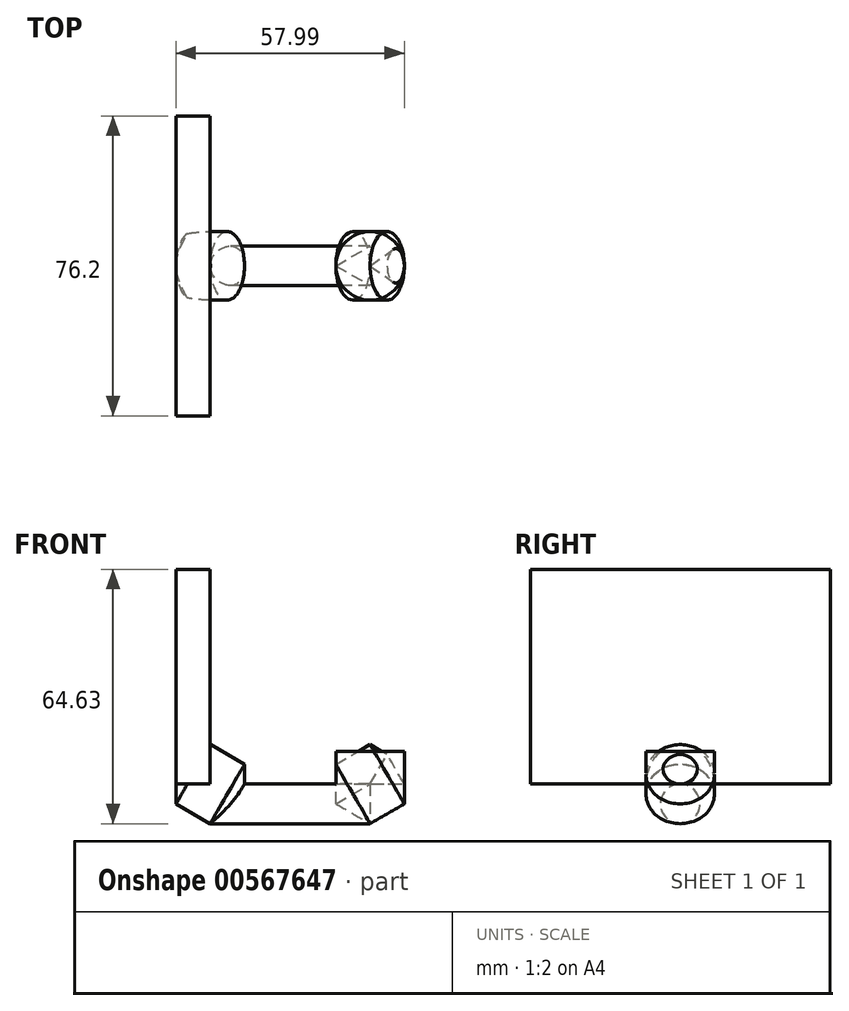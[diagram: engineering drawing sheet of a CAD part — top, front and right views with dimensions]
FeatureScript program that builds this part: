
annotation { "Feature Type Name" : "Feature", "Feature Type Description" : "" }
export const myFeature = defineFeature(function(context is Context, id is Id, definition is map)
    precondition{}
    {
        {
            var Q0;
            Q0=qCreatedBy(makeId("Front.planeOp"),FACE);
            var sketch = newSketch(context, id + "F0", { "sketchPlane" : qUnion([Q0])});
            skLineSegment(sketch, "E0", {"start": v(0, 5.02) * mm, "end": v(0, 64.63) * mm});
            skLineSegment(sketch, "E1", {"start": v(0, 64.63) * mm, "end": v(8.69, 64.63) * mm});
            skLineSegment(sketch, "E2", {"start": v(8.69, 64.63) * mm, "end": v(8.69, 0) * mm});
            skLineSegment(sketch, "E3", {"start": v(49.3, 0) * mm, "end": v(8.69, 0) * mm});
            skLineSegment(sketch, "E4", {"start": v(49.3, 5.02) * mm, "end": v(40.62, 5.02) * mm});
            skLineSegment(sketch, "E5", {"start": v(58, 10.05) * mm, "end": v(58, 5.02) * mm});
            skLineSegment(sketch, "E6", {"start": v(49.3, 18.37) * mm, "end": v(58, 18.37) * mm});
            skLineSegment(sketch, "E7", {"start": v(49.3, 5.02) * mm, "end": v(49.3, 18.37) * mm});
            skLineSegment(sketch, "E8", {"start": v(0, 5.02) * mm, "end": v(8.69, 5.02) * mm});
            skLineSegment(sketch, "E9", {"start": v(49.3, 0) * mm, "end": v(49.3, 5.02) * mm});
            skLineSegment(sketch, "E10", {"start": v(58, 10.05) * mm, "end": v(49.3, 10.05) * mm});
            skLineSegment(sketch, "E11", {"start": v(58, 18.37) * mm, "end": v(58, 10.05) * mm});
            skLineSegment(sketch, "E12", {"start": v(0, 5.02) * mm, "end": v(8.69, 0) * mm});
            skLineSegment(sketch, "E13", {"start": v(58, 5.02) * mm, "end": v(49.3, 0) * mm});
            skLineSegment(sketch, "E14.trimOffspring", {"start": v(17.37, 5.02) * mm, "end": v(8.69, 5.02) * mm});
            skLineSegment(sketch, "E15", {"start": v(17.37, 5.02) * mm, "end": v(40.62, 5.02) * mm});
            skLineSegment(sketch, "E16", {"start": v(8.69, 10.05) * mm, "end": v(17.37, 5.02) * mm});
            skLineSegment(sketch, "E17", {"start": v(49.3, 10.05) * mm, "end": v(40.62, 5.02) * mm});
            skLineSegment(sketch, "E18.trimOffspring", {"start": v(8.69, 10.05) * mm, "end": v(0, 10.05) * mm});
            skPoint(sketch, "E19.orphan", {"position": v(58, 0) * mm});
            skLineSegment(sketch, "E20", {"start": v(17.37, 5.02) * mm, "end": v(8.69, 0) * mm});
            skLineSegment(sketch, "E21", {"start": v(8.69, 10.05) * mm, "end": v(0, 5.02) * mm});
            skLineSegment(sketch, "E22", {"start": v(49.3, 10.05) * mm, "end": v(58, 5.02) * mm});
            skLineSegment(sketch, "E23", {"start": v(40.62, 5.02) * mm, "end": v(49.3, 0) * mm});
            skSolve(sketch);
        }
        {
            var Q0;
            {var subQ2=sQuery(id+"F0.wireOp",EDGE,"E18.trimOffspring");Q0=makeQuery(id+"F0.imprint","IMPRINT",FACE,{"disambiguationData":[TD([[makeQuery(id+"F0.imprint","IMPRINT",EDGE,{"derivedFrom":subQ2}),1.0]])]});}
            var Q1;
            {var subQ0=sQuery(id+"F0.wireOp",EDGE,"E14.trimOffspring");Q1=makeQuery(id+"F0.imprint","IMPRINT",FACE,{"disambiguationData":[TD([[makeQuery(id+"F0.imprint","IMPRINT",EDGE,{"derivedFrom":subQ0}),-1.0]])]});}
            var Q2;
            {var subQ0=sQuery(id+"F0.wireOp",EDGE,"E8");Q2=makeQuery(id+"F0.imprint","IMPRINT",FACE,{"disambiguationData":[TD([[makeQuery(id+"F0.imprint","IMPRINT",EDGE,{"derivedFrom":subQ0}),1.0]])]});}
            var Q3;
            {var subQ2=sQuery(id+"F0.wireOp",EDGE,"E8");Q3=makeQuery(id+"F0.imprint","IMPRINT",FACE,{"disambiguationData":[TD([[makeQuery(id+"F0.imprint","IMPRINT",EDGE,{"derivedFrom":subQ2}),-1.0]])]});}
            var Q4;
            {var subQ2=sQuery(id+"F0.wireOp",EDGE,"E14.trimOffspring");Q4=makeQuery(id+"F0.imprint","IMPRINT",FACE,{"disambiguationData":[TD([[makeQuery(id+"F0.imprint","IMPRINT",EDGE,{"derivedFrom":subQ2}),1.0]])]});}
            var Q5;
            Q5=sQuery(id+"F0.wireOp",EDGE,"E16");
            revolve(context, id + "F1", {"entities" : qUnion([Q0, Q1, Q2, Q3, Q4]), "axis" : qUnion([Q5]), "revolveType" : RevolveType.FULL});
        }
        {
            var Q0;
            Q0=makeQuery(id+"F0.imprint","IMPRINT",FACE,{"disambiguationData":[TD([[makeQuery(id+"F0.imprint","IMPRINT",EDGE,{"derivedFrom":sQuery(id+"F0.wireOp",EDGE,"E4")}),1.0]])]});
            var Q1;
            {var subQ0=sQuery(id+"F0.wireOp",EDGE,"E4");Q1=makeQuery(id+"F0.imprint","IMPRINT",FACE,{"disambiguationData":[TD([[makeQuery(id+"F0.imprint","IMPRINT",EDGE,{"derivedFrom":subQ0}),-1.0]])]});}
            var Q2;
            {var subQ0=sQuery(id+"F0.wireOp",EDGE,"E9");Q2=makeQuery(id+"F0.imprint","IMPRINT",FACE,{"disambiguationData":[TD([[makeQuery(id+"F0.imprint","IMPRINT",EDGE,{"derivedFrom":subQ0}),-1.0]])]});}
            var Q3;
            Q3=makeQuery(id+"F0.imprint","IMPRINT",FACE,{"disambiguationData":[TD([[makeQuery(id+"F0.imprint","IMPRINT",EDGE,{"derivedFrom":sQuery(id+"F0.wireOp",EDGE,"E5")}),-1.0]])]});
            var Q4;
            Q4=sQuery(id+"F0.wireOp",EDGE,"E17");
            revolve(context, id + "F2", {"entities" : qUnion([Q0, Q1, Q2, Q3]), "axis" : qUnion([Q4]), "revolveType" : RevolveType.FULL});
        }
        {
            var Q0;
            Q0=makeQuery(id+"F0.imprint","IMPRINT",FACE,{"disambiguationData":[TD([[makeQuery(id+"F0.imprint","IMPRINT",EDGE,{"derivedFrom":sQuery(id+"F0.wireOp",EDGE,"E3")}),-1.0]])]});
            var Q1;
            Q1=sQuery(id+"F0.wireOp",EDGE,"E15");
            revolve(context, id + "F3", {"entities" : qUnion([Q0]), "axis" : qUnion([Q1]), "revolveType" : RevolveType.FULL});
        }
        {
            var Q0;
            {var subQ0=sQuery(id+"F0.wireOp",EDGE,"E6");Q0=makeQuery(id+"F0.imprint","IMPRINT",FACE,{"disambiguationData":[TD([[makeQuery(id+"F0.imprint","IMPRINT",EDGE,{"derivedFrom":subQ0}),-1.0]])]});}
            var Q1;
            Q1=sQuery(id+"F0.wireOp",EDGE,"E7");
            revolve(context, id + "F4", {"entities" : qUnion([Q0]), "axis" : qUnion([Q1]), "revolveType" : RevolveType.FULL});
        }
        {
            var Q0;
            {var subQ0=sQuery(id+"F0.wireOp",EDGE,"E1");Q0=makeQuery(id+"F0.imprint","IMPRINT",FACE,{"disambiguationData":[TD([[makeQuery(id+"F0.imprint","IMPRINT",EDGE,{"derivedFrom":subQ0}),-1.0]])]});}
            extrude(context, id + "F5", {"entities" : qUnion([Q0]), "operationType" : NewBodyOperationType.ADD, "endBound" : BoundingType.SYMMETRIC, "depth" : 76.2 * mm, "offsetDistance" : 25.4 * mm});
        }
    });
